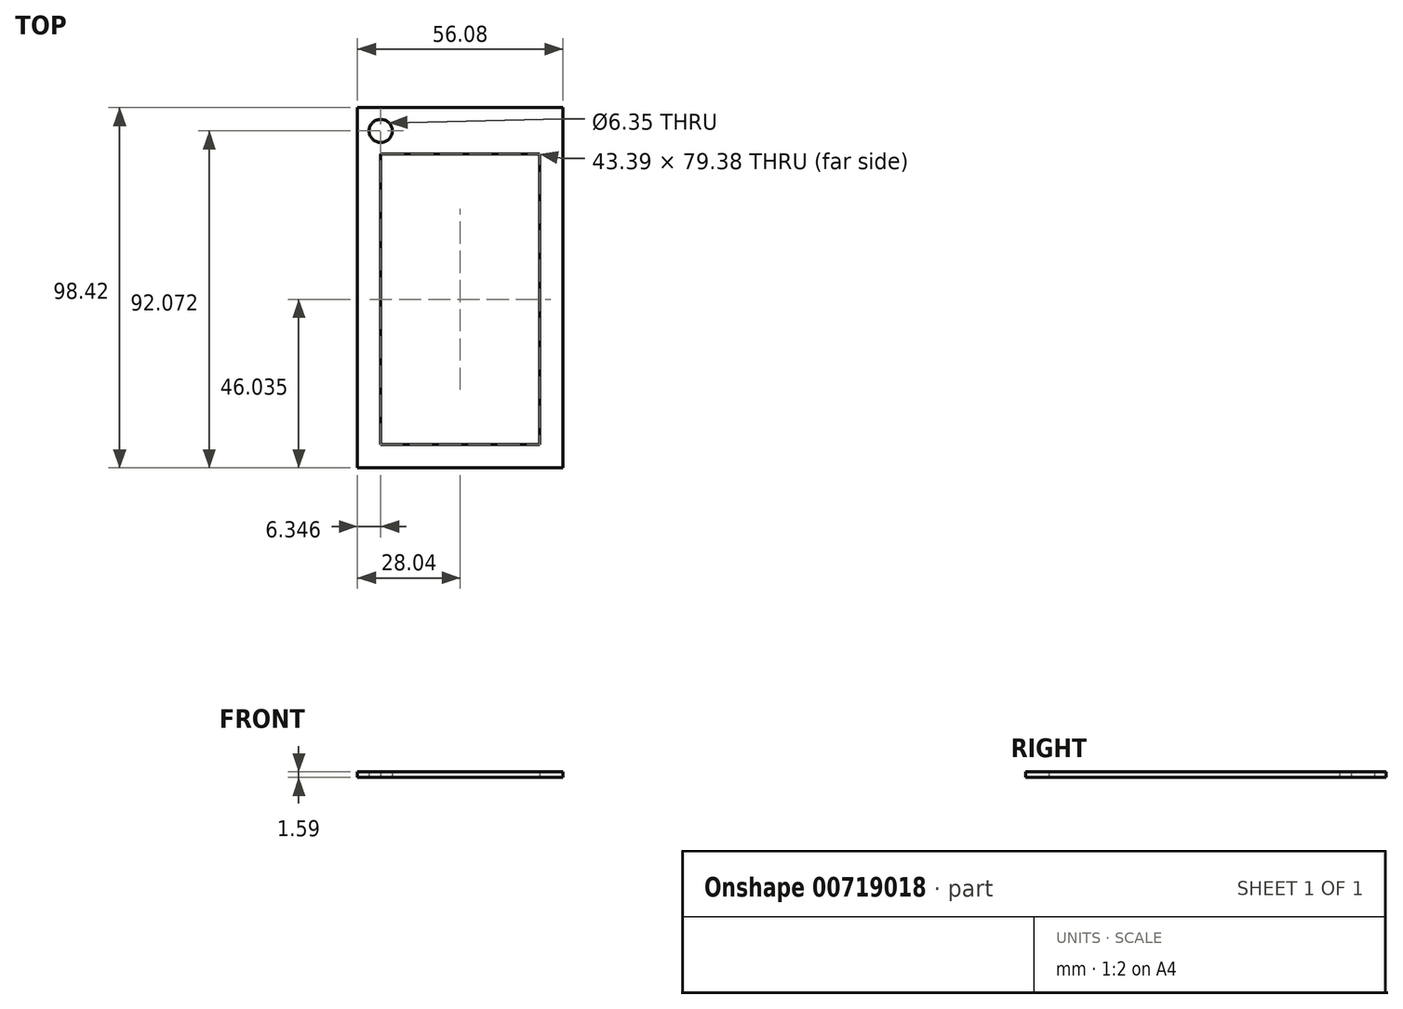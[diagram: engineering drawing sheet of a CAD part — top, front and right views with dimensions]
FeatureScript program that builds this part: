
annotation { "Feature Type Name" : "Feature", "Feature Type Description" : "" }
export const myFeature = defineFeature(function(context is Context, id is Id, definition is map)
    precondition{}
    {
        {
            var Q0;
            Q0=qCreatedBy(makeId("Top.planeOp"),FACE);
            var sketch = newSketch(context, id + "F0", { "sketchPlane" : qUnion([Q0])});
            skPoint(sketch, "E0.middle", {"position": v(0, 0) * mm});
            skLineSegment(sketch, "E1.bottom", {"start": v(28.04, -49.21) * mm, "end": v(-28.04, -49.21) * mm});
            skLineSegment(sketch, "E1.top", {"start": v(28.04, 49.21) * mm, "end": v(-28.04, 49.21) * mm});
            skLineSegment(sketch, "E1.left", {"start": v(28.04, -49.21) * mm, "end": v(28.04, 49.21) * mm});
            skLineSegment(sketch, "E1.right", {"start": v(-28.04, -49.21) * mm, "end": v(-28.04, 49.21) * mm});
            skPoint(sketch, "E0.left.end.orphan", {"position": v(18.64, 35.28) * mm});
            skPoint(sketch, "E0.bottom.start.orphan", {"position": v(18.64, -35.28) * mm});
            skPoint(sketch, "E0.right.end.orphan", {"position": v(-18.64, 35.28) * mm});
            skPoint(sketch, "E0.right.start.orphan", {"position": v(-18.64, -35.28) * mm});
            skLineSegment(sketch, "E2.bottom", {"start": v(-28.04, 49.21) * mm, "end": v(28.04, 49.21) * mm});
            skLineSegment(sketch, "E2.left", {"start": v(-28.04, 49.21) * mm, "end": v(-28.04, 35.28) * mm});
            skLineSegment(sketch, "E2.right", {"start": v(28.04, 49.21) * mm, "end": v(28.04, 35.28) * mm});
            skLineSegment(sketch, "E3.bottom", {"start": v(0, 49.21) * mm, "end": v(28.04, 49.21) * mm});
            skLineSegment(sketch, "E3.left", {"start": v(0, 36.51) * mm, "end": v(0, 35.28) * mm});
            skLineSegment(sketch, "E4", {"start": v(0, 36.51) * mm, "end": v(21.7, 36.51) * mm});
            skLineSegment(sketch, "E5", {"start": v(0, 36.51) * mm, "end": v(-21.7, 36.51) * mm});
            skPoint(sketch, "E6.start.orphan", {"position": v(-28.04, 0) * mm});
            skLineSegment(sketch, "E7", {"start": v(-21.7, 0) * mm, "end": v(-21.7, -42.86) * mm});
            skLineSegment(sketch, "E8", {"start": v(-21.7, 0) * mm, "end": v(-21.7, 36.51) * mm});
            skLineSegment(sketch, "E9", {"start": v(28.04, 0) * mm, "end": v(21.7, 0) * mm});
            skLineSegment(sketch, "E10", {"start": v(21.7, 0) * mm, "end": v(21.7, -42.86) * mm});
            skLineSegment(sketch, "E11", {"start": v(21.7, 0) * mm, "end": v(21.7, 36.51) * mm});
            skPoint(sketch, "E12.endSnap0", {"position": v(0, -49.21) * mm});
            skLineSegment(sketch, "E13", {"start": v(0, -42.86) * mm, "end": v(21.7, -42.86) * mm});
            skLineSegment(sketch, "E14", {"start": v(0, -42.86) * mm, "end": v(-21.7, -42.86) * mm});
            skPoint(sketch, "E12.start.orphan", {"position": v(0, -49.21) * mm});
            skCircle(sketch, "E15", {"center": v(-21.7, 42.86) * mm, "radius": 3.18 * mm});
            skPoint(sketch, "E16.orphan", {"position": v(-21.7, 49.21) * mm});
            skSolve(sketch);
        }
        {
            var Q0;
            Q0 = qSketchRegion(id + "F0", true);
            extrude(context, id + "F1", {"entities" : qUnion([Q0]), "depth" : 1.59 * mm, "offsetDistance" : 25.4 * mm});
        }
    });
